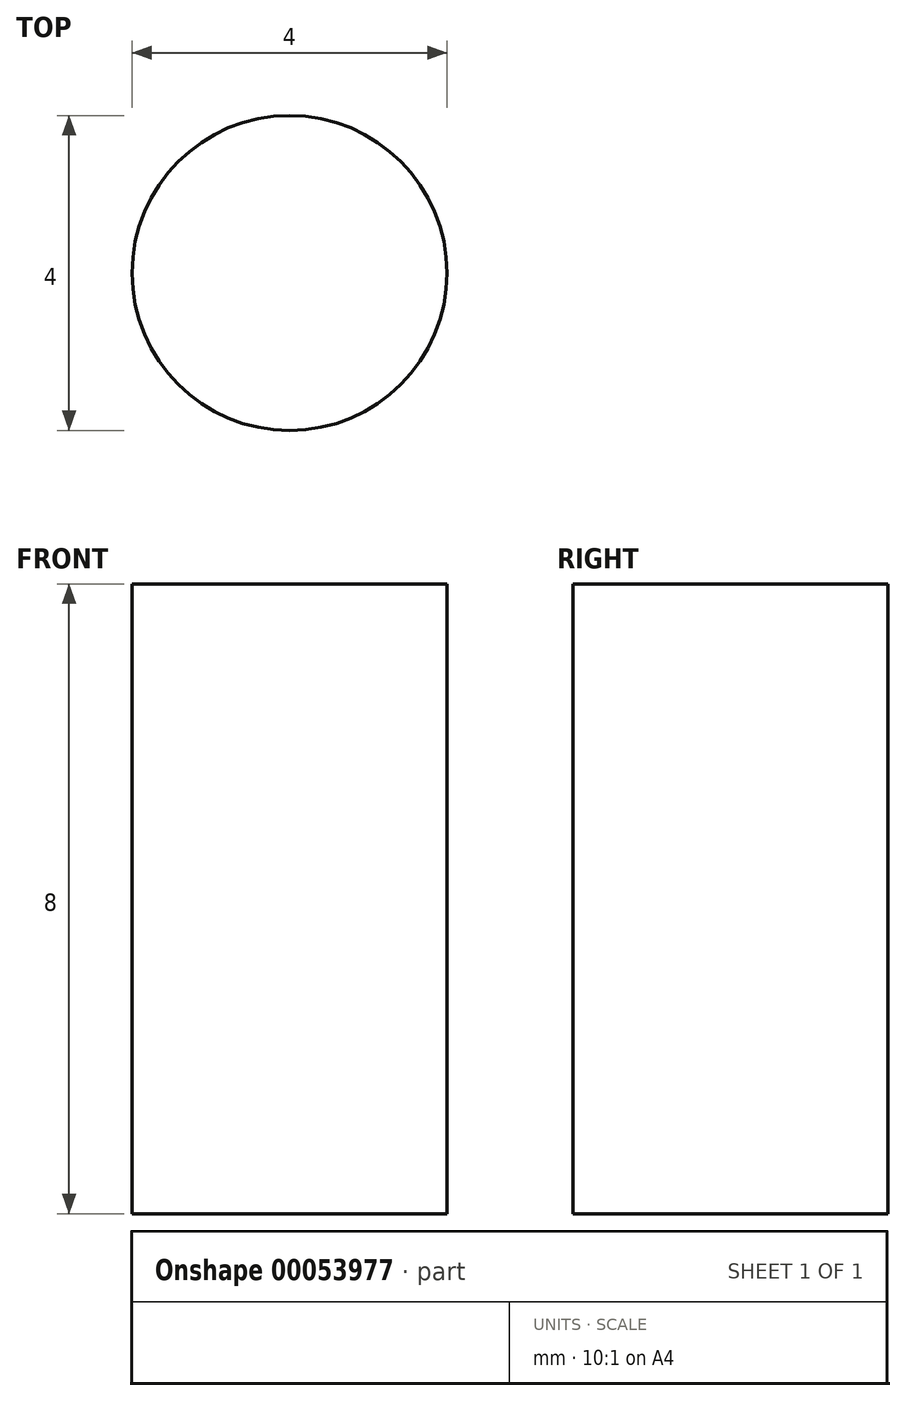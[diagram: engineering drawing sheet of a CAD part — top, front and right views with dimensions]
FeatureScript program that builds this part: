
annotation { "Feature Type Name" : "Feature", "Feature Type Description" : "" }
export const myFeature = defineFeature(function(context is Context, id is Id, definition is map)
    precondition{}
    {
        {
            var Q0;
            Q0=qCreatedBy(makeId("Top.planeOp"),FACE);
            var sketch = newSketch(context, id + "F0", { "sketchPlane" : qUnion([Q0])});
            skCircle(sketch, "E0", {"center": v(0, 0) * mm, "radius": 2 * mm});
            skSolve(sketch);
        }
        {
            var Q0;
            Q0=sQuery(id+"F0.wireOp",EDGE,"E0");
            extrude(context, id + "F1", {"bodyType" : ToolBodyType.SURFACE, "surfaceEntities" : qUnion([Q0]), "depth" : 8 * mm});
        }
    });
